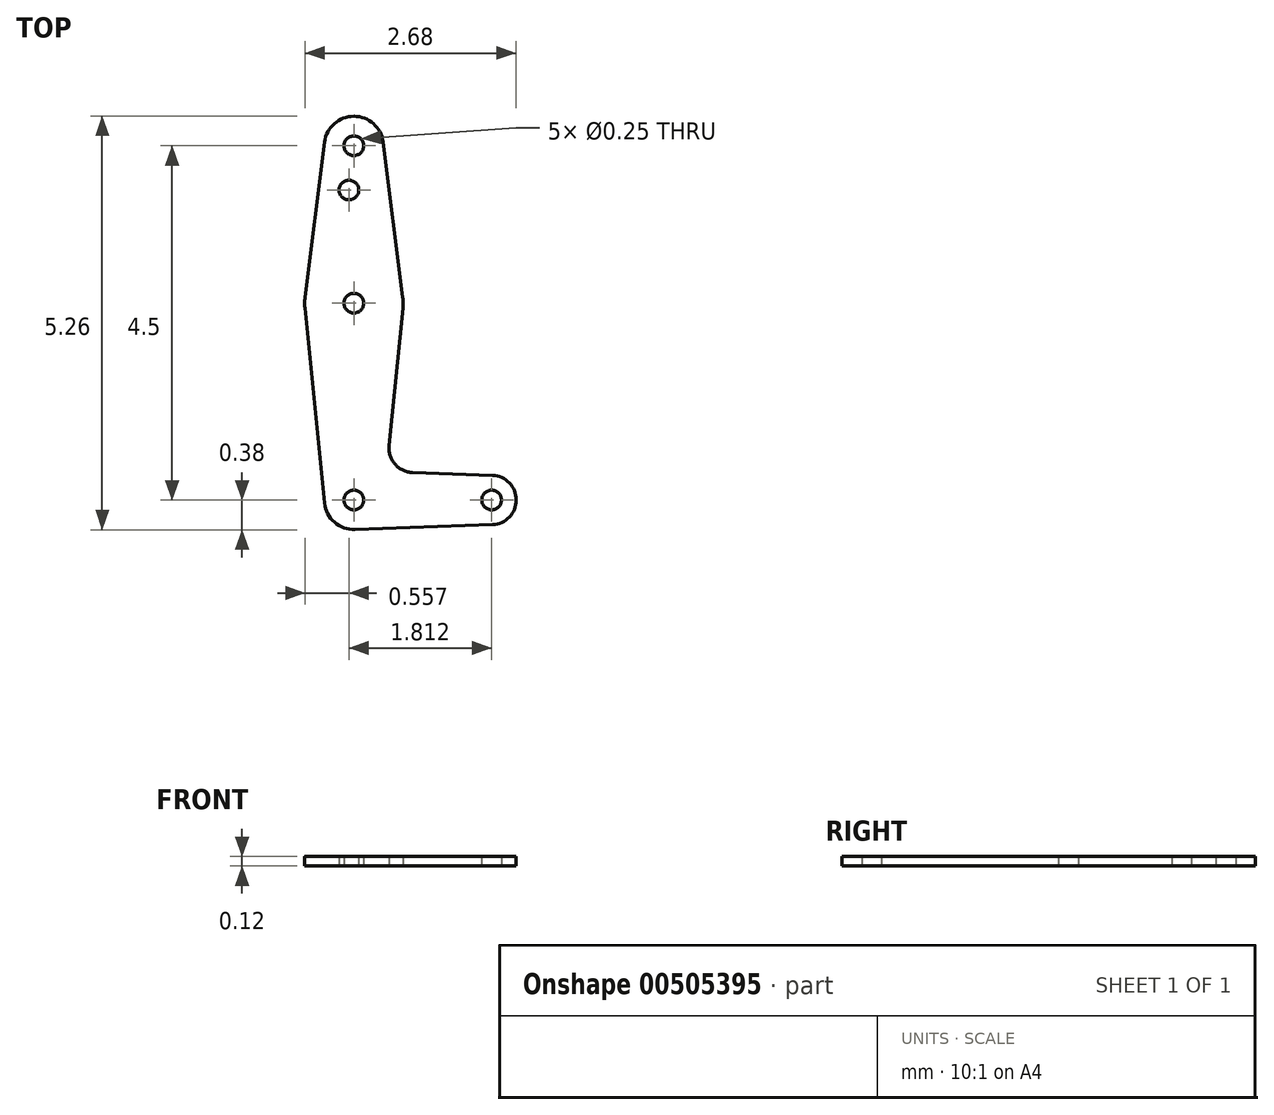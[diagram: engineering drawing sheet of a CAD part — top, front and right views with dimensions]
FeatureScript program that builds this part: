
annotation { "Feature Type Name" : "Feature", "Feature Type Description" : "" }
export const myFeature = defineFeature(function(context is Context, id is Id, definition is map)
    precondition{}
    {
        {
            var Q0;
            Q0=qCreatedBy(makeId("Top.planeOp"),FACE);
            var sketch = newSketch(context, id + "F0", { "sketchPlane" : qUnion([Q0])});
            skCircle(sketch, "E0", {"center": v(0, 0) * mm, "radius": 0.37 * mm});
            skCircle(sketch, "E1", {"center": v(0, -2) * mm, "radius": 0.62 * mm});
            skLineSegment(sketch, "E2", {"start": v(0, 0) * mm, "end": v(0, -4.5) * mm, "construction": true});
            skCircle(sketch, "E3", {"center": v(0, -4.5) * mm, "radius": 0.38 * mm});
            skLineSegment(sketch, "E4", {"start": v(0, -4.5) * mm, "end": v(1.75, -4.5) * mm, "construction": true});
            skCircle(sketch, "E5", {"center": v(1.75, -4.5) * mm, "radius": 0.31 * mm});
            skLineSegment(sketch, "E6", {"start": v(0.37, 0.05) * mm, "end": v(0.63, -2) * mm});
            skLineSegment(sketch, "E7", {"start": v(-0.37, 0.05) * mm, "end": v(-0.62, -1.92) * mm});
            skLineSegment(sketch, "E8", {"start": v(-0.62, -2.06) * mm, "end": v(-0.37, -4.54) * mm});
            skPoint(sketch, "E9.startSnap0", {"position": v(0, -2.25) * mm});
            skLineSegment(sketch, "E10", {"start": v(0.62, -2.06) * mm, "end": v(0.45, -3.8) * mm});
            skLineSegment(sketch, "E11", {"start": v(0.01, -4.87) * mm, "end": v(1.76, -4.81) * mm});
            skLineSegment(sketch, "E12", {"start": v(0.75, -4.15) * mm, "end": v(1.76, -4.19) * mm});
            skCircle(sketch, "E13", {"center": v(0, 0) * mm, "radius": 0.12 * mm});
            skCircle(sketch, "E14", {"center": v(0, -2) * mm, "radius": 0.12 * mm});
            skCircle(sketch, "E15", {"center": v(0, -4.5) * mm, "radius": 0.12 * mm});
            skCircle(sketch, "E16", {"center": v(1.75, -4.5) * mm, "radius": 0.12 * mm});
            skCircle(sketch, "E17", {"center": v(-0.06, -0.56) * mm, "radius": 0.12 * mm});
            skArc(sketch, "E18.filletArc", {"start": v(0.45, -3.8) * mm, "mid": v(0.52, -4.04) * mm, "end": v(0.75, -4.15) * mm});
            skSolve(sketch);
        }
        {
            var Q0;
            Q0 = qSketchRegion(id + "F0", true);
            extrude(context, id + "F1", {"entities" : qUnion([Q0]), "depth" : 0.12 * mm});
        }
    });
